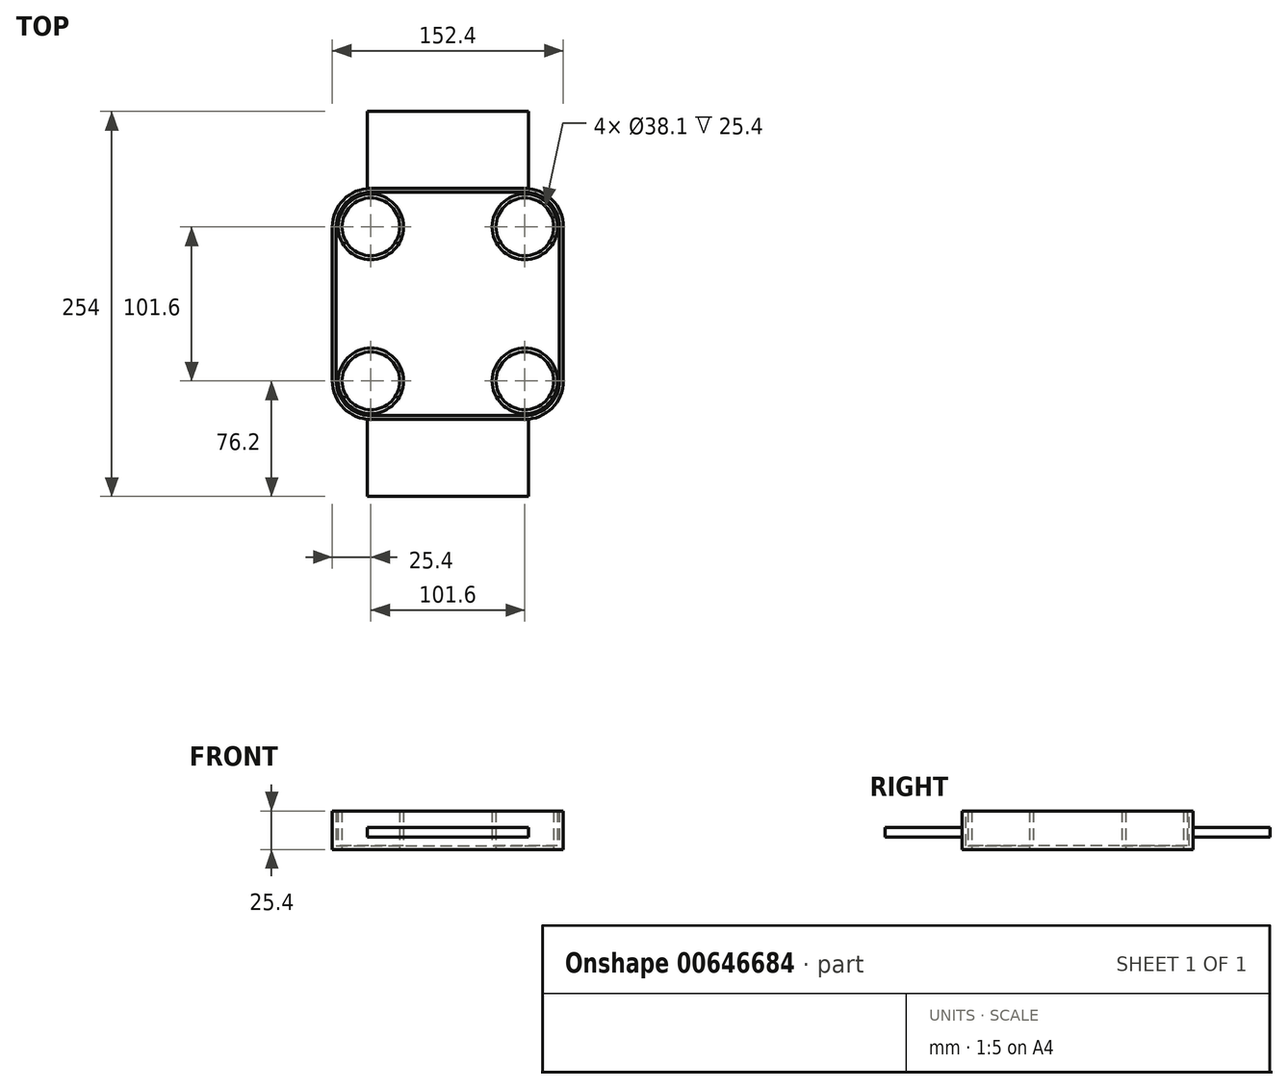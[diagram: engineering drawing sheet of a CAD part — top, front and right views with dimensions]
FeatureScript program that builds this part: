
annotation { "Feature Type Name" : "Feature", "Feature Type Description" : "" }
export const myFeature = defineFeature(function(context is Context, id is Id, definition is map)
    precondition{}
    {
        {
            var Q0;
            Q0=qCreatedBy(makeId("Top.planeOp"),FACE);
            var sketch = newSketch(context, id + "F0", { "sketchPlane" : qUnion([Q0])});
            skLineSegment(sketch, "E0.bottom", {"start": v(-76.2, 76.2) * mm, "end": v(76.2, 76.2) * mm});
            skLineSegment(sketch, "E0.top", {"start": v(-76.2, -76.2) * mm, "end": v(76.2, -76.2) * mm});
            skLineSegment(sketch, "E0.left", {"start": v(-76.2, 76.2) * mm, "end": v(-76.2, -76.2) * mm});
            skLineSegment(sketch, "E0.right", {"start": v(76.2, 76.2) * mm, "end": v(76.2, -76.2) * mm});
            skPoint(sketch, "E0.middle", {"position": v(0, 0) * mm});
            skCircle(sketch, "E1", {"center": v(-50.8, 50.8) * mm, "radius": 19.05 * mm});
            skCircle(sketch, "E2.MirrorC", {"center": v(-50.8, -50.8) * mm, "radius": 19.05 * mm});
            skCircle(sketch, "E3.MirrorC", {"center": v(50.8, 50.8) * mm, "radius": 19.05 * mm});
            skCircle(sketch, "E4.MirrorC", {"center": v(50.8, -50.8) * mm, "radius": 19.05 * mm});
            skSolve(sketch);
        }
        {
            var Q0;
            Q0=makeQuery(id+"F0.imprint","IMPRINT",FACE,{"disambiguationData":[TD([[makeQuery(id+"F0.imprint","IMPRINT",EDGE,{"derivedFrom":sQuery(id+"F0.wireOp",EDGE,"E0.bottom")}),-1.0]])]});
            extrude(context, id + "F1", {"entities" : qUnion([Q0]), "depth" : 25.4 * mm, "offsetDistance" : 25.4 * mm});
        }
        {
            var Q0;
            Q0=makeQuery(id+"F1.opExtrude","SWEPT_FACE",FACE,{"disambiguationData":[OSD([sQuery(id+"F0.wireOp",EDGE,"E0.top")])]});
            var sketch = newSketch(context, id + "F2", { "sketchPlane" : qUnion([Q0])});
            skLineSegment(sketch, "E5.bottom", {"start": v(53.1, 14.53) * mm, "end": v(-53.1, 14.53) * mm});
            skLineSegment(sketch, "E5.top", {"start": v(53.1, 8.2) * mm, "end": v(-53.1, 8.2) * mm});
            skLineSegment(sketch, "E5.left", {"start": v(53.1, 14.53) * mm, "end": v(53.1, 8.2) * mm});
            skLineSegment(sketch, "E5.right", {"start": v(-53.1, 14.53) * mm, "end": v(-53.1, 8.2) * mm});
            skPoint(sketch, "E5.middle", {"position": v(0, 11.37) * mm});
            skSolve(sketch);
        }
        {
            var Q0;
            Q0 = qSketchRegion(id + "F2", true);
            extrude(context, id + "F3", {"entities" : qUnion([Q0]), "depth" : 50.8 * mm, "offsetDistance" : 25.4 * mm});
        }
        {
            var Q0;
            Q0=makeQuery(id+"F3.opExtrude","SWEPT_BODY",BODY,{"disambiguationData":[OSD([sQuery(id+"F2.wireOp",EDGE,"E5.bottom"),sQuery(id+"F2.wireOp",EDGE,"E5.top"),sQuery(id+"F2.wireOp",EDGE,"E5.left"),sQuery(id+"F2.wireOp",EDGE,"E5.right")])]});
            var Q1;
            Q1=qCreatedBy(makeId("Front.planeOp"),FACE);
            mirror(context, id + "F4", {"entities" : qUnion([Q0]), "mirrorPlane" : qUnion([Q1])});
        }
        {
            var Q0;
            Q0=makeQuery(id+"F1.opExtrude","SWEPT_EDGE",EDGE,{"disambiguationData":[OSD([sQuery(id+"F0.wireOp",EDGE,"E0.top"),sQuery(id+"F0.wireOp",EDGE,"E0.right")])]});
            var Q1;
            Q1=makeQuery(id+"F1.opExtrude","SWEPT_EDGE",EDGE,{"disambiguationData":[OSD([sQuery(id+"F0.wireOp",EDGE,"E0.bottom"),sQuery(id+"F0.wireOp",EDGE,"E0.right")])]});
            var Q2;
            Q2=makeQuery(id+"F1.opExtrude","SWEPT_EDGE",EDGE,{"disambiguationData":[OSD([sQuery(id+"F0.wireOp",EDGE,"E0.top"),sQuery(id+"F0.wireOp",EDGE,"E0.left")])]});
            var Q3;
            Q3=makeQuery(id+"F1.opExtrude","SWEPT_EDGE",EDGE,{"disambiguationData":[OSD([sQuery(id+"F0.wireOp",EDGE,"E0.bottom"),sQuery(id+"F0.wireOp",EDGE,"E0.left")])]});
            fillet(context, id + "F5", {"entities" : qUnion([Q0, Q1, Q2, Q3]), "radius" : 25.4 * mm, "tangentPropagation" : true, "allowEdgeOverflow" : false});
        }
        {
            var Q0;
            Q0=makeQuery(id+"F1.opExtrude","CAP_FACE",FACE,{"disambiguationData":[OSD([sQuery(id+"F0.wireOp",EDGE,"E0.bottom"),sQuery(id+"F0.wireOp",EDGE,"E0.top"),sQuery(id+"F0.wireOp",EDGE,"E0.left"),sQuery(id+"F0.wireOp",EDGE,"E0.right"),sQuery(id+"F0.wireOp",EDGE,"E1"),sQuery(id+"F0.wireOp",EDGE,"E2.MirrorC"),sQuery(id+"F0.wireOp",EDGE,"E3.MirrorC"),sQuery(id+"F0.wireOp",EDGE,"E4.MirrorC")])],"isStart":false});
            shell(context, id + "F6", {"entities" : qUnion([Q0]), "thickness" : 2.54 * mm});
        }
    });
